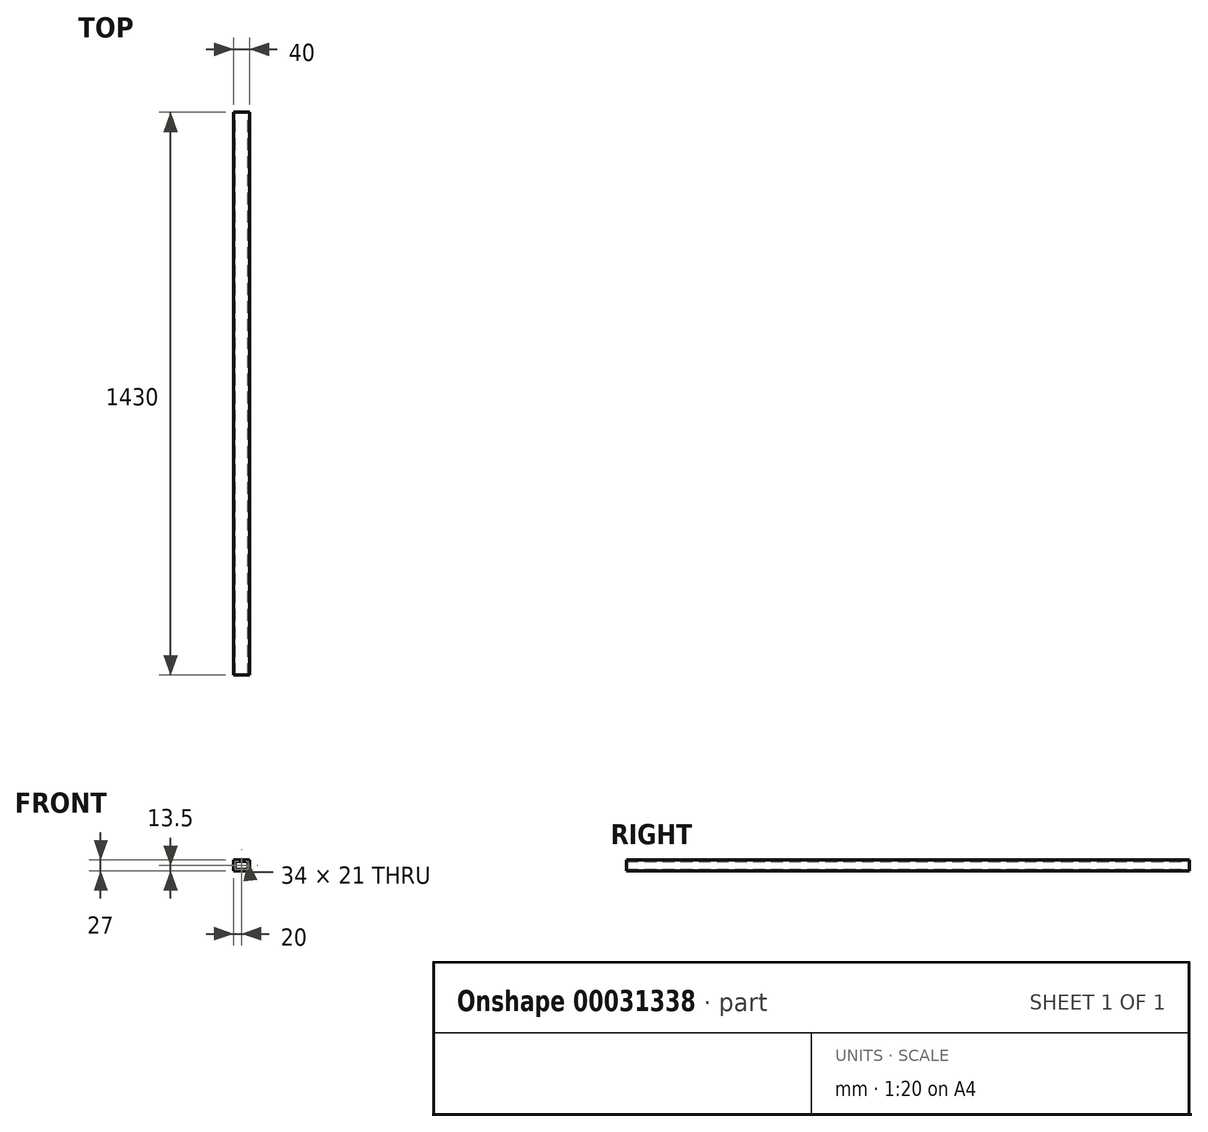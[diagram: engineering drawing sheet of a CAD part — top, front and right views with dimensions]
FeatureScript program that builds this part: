
annotation { "Feature Type Name" : "Feature", "Feature Type Description" : "" }
export const myFeature = defineFeature(function(context is Context, id is Id, definition is map)
    precondition{}
    {
        {
            var Q0;
            Q0=qCreatedBy(makeId("Front.planeOp"),FACE);
            var sketch = newSketch(context, id + "F0", { "sketchPlane" : qUnion([Q0])});
            skLineSegment(sketch, "E0.rect.bottom", {"start": v(20, -13.5) * mm, "end": v(-20, -13.5) * mm});
            skLineSegment(sketch, "E0.rect.top", {"start": v(20, 13.5) * mm, "end": v(-20, 13.5) * mm});
            skLineSegment(sketch, "E0.rect.left", {"start": v(20, -13.5) * mm, "end": v(20, 13.5) * mm});
            skLineSegment(sketch, "E0.rect.right", {"start": v(-20, -13.5) * mm, "end": v(-20, 13.5) * mm});
            skPoint(sketch, "E0.rect.middle", {"position": v(0, 0) * mm});
            skLineSegment(sketch, "E1.rect.bottom", {"start": v(17, -10.5) * mm, "end": v(-17, -10.5) * mm});
            skLineSegment(sketch, "E1.rect.top", {"start": v(17, 10.5) * mm, "end": v(-17, 10.5) * mm});
            skLineSegment(sketch, "E1.rect.left", {"start": v(17, -10.5) * mm, "end": v(17, 10.5) * mm});
            skLineSegment(sketch, "E1.rect.right", {"start": v(-17, -10.5) * mm, "end": v(-17, 10.5) * mm});
            skSolve(sketch);
        }
        {
            var Q0;
            Q0=makeQuery(id+"F0.imprint","IMPRINT",FACE,{"disambiguationData":[TD([[makeQuery(id+"F0.imprint","IMPRINT",EDGE,{"derivedFrom":sQuery(id+"F0.wireOp",EDGE,"E0.rect.bottom")}),-1.0]])]});
            extrude(context, id + "F1", {"entities" : qUnion([Q0]), "endBound" : BoundingType.SYMMETRIC, "depth" : 1430 * mm});
        }
    });
